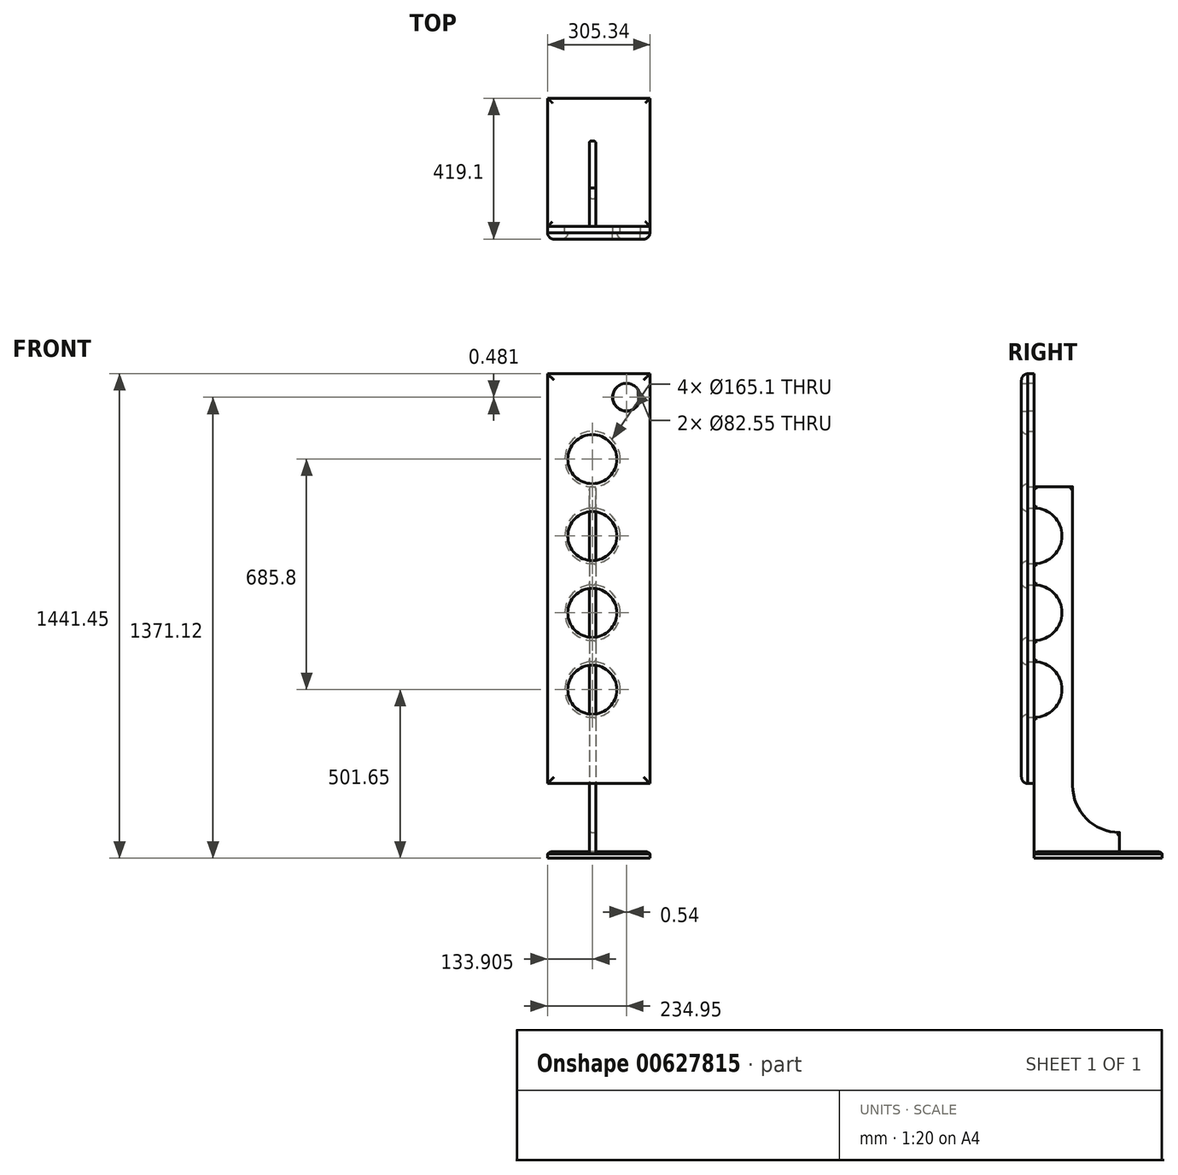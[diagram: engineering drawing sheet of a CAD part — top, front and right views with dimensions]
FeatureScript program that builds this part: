
annotation { "Feature Type Name" : "Feature", "Feature Type Description" : "" }
export const myFeature = defineFeature(function(context is Context, id is Id, definition is map)
    precondition{}
    {
        {
            var Q0;
            Q0=qCreatedBy(makeId("Front.planeOp"),FACE);
            var sketch = newSketch(context, id + "F0", { "sketchPlane" : qUnion([Q0])});
            skLineSegment(sketch, "E0.bottom", {"start": v(0, 0) * mm, "end": v(304.8, 0) * mm});
            skLineSegment(sketch, "E0.top", {"start": v(0, 1219.2) * mm, "end": v(304.8, 1219.2) * mm});
            skLineSegment(sketch, "E0.left", {"start": v(0, 0) * mm, "end": v(0, 1219.2) * mm});
            skLineSegment(sketch, "E0.right", {"start": v(304.8, 0) * mm, "end": v(304.8, 1219.2) * mm});
            skCircle(sketch, "E1", {"center": v(133.36, 965.2) * mm, "radius": 82.55 * mm});
            skCircle(sketch, "E2", {"center": v(133.36, 736.27) * mm, "radius": 82.55 * mm});
            skCircle(sketch, "E3", {"center": v(133.36, 508) * mm, "radius": 82.55 * mm});
            skCircle(sketch, "E4", {"center": v(133.36, 279.4) * mm, "radius": 82.55 * mm});
            skCircle(sketch, "E5", {"center": v(234.95, 1149.35) * mm, "radius": 41.28 * mm});
            skSolve(sketch);
        }
        {
            var Q0;
            Q0=makeQuery(id+"F0.imprint","IMPRINT",FACE,{"disambiguationData":[TD([[makeQuery(id+"F0.imprint","IMPRINT",EDGE,{"derivedFrom":sQuery(id+"F0.wireOp",EDGE,"E0.bottom")}),1.0]])]});
            extrude(context, id + "F1", {"entities" : qUnion([Q0]), "depth" : 19.05 * mm, "offsetDistance" : 25.4 * mm});
        }
        {
            var Q0;
            Q0=makeQuery(id+"F1.opExtrude","CAP_FACE",FACE,{"disambiguationData":[OSD([sQuery(id+"F0.wireOp",EDGE,"E0.bottom"),sQuery(id+"F0.wireOp",EDGE,"E0.top"),sQuery(id+"F0.wireOp",EDGE,"E0.left"),sQuery(id+"F0.wireOp",EDGE,"E0.right"),sQuery(id+"F0.wireOp",EDGE,"E1"),sQuery(id+"F0.wireOp",EDGE,"E2"),sQuery(id+"F0.wireOp",EDGE,"E3"),sQuery(id+"F0.wireOp",EDGE,"E4"),sQuery(id+"F0.wireOp",EDGE,"E5")])],"isStart":false});
            var sketch = newSketch(context, id + "F2", { "sketchPlane" : qUnion([Q0])});
            skLineSegment(sketch, "E6.bottom", {"start": v(-0.54, -0.48) * mm, "end": v(304.26, -0.48) * mm});
            skLineSegment(sketch, "E6.top", {"start": v(-0.54, 1218.72) * mm, "end": v(304.26, 1218.72) * mm});
            skLineSegment(sketch, "E6.left", {"start": v(-0.54, -0.48) * mm, "end": v(-0.54, 1218.72) * mm});
            skLineSegment(sketch, "E6.right", {"start": v(304.26, -0.48) * mm, "end": v(304.26, 1218.72) * mm});
            skCircle(sketch, "E7", {"center": v(132.82, 964.72) * mm, "radius": 73.03 * mm});
            skCircle(sketch, "E8", {"center": v(132.82, 735.79) * mm, "radius": 73.03 * mm});
            skCircle(sketch, "E9", {"center": v(132.82, 507.52) * mm, "radius": 73.03 * mm});
            skCircle(sketch, "E10", {"center": v(132.82, 278.92) * mm, "radius": 73.03 * mm});
            skCircle(sketch, "E11", {"center": v(234.4, 1148.87) * mm, "radius": 41.28 * mm});
            skSolve(sketch);
        }
        {
            var Q0;
            Q0 = qSketchRegion(id + "F2", true);
            extrude(context, id + "F3", {"entities" : qUnion([Q0]), "depth" : 19.05 * mm, "offsetDistance" : 25.4 * mm});
        }
        {
            var Q0;
            Q0=makeQuery(id+"F3.opExtrude","CAP_EDGE",EDGE,{"disambiguationData":[OSD([sQuery(id+"F2.wireOp",EDGE,"E7")])],"isStart":false});
            var Q1;
            Q1=makeQuery(id+"F3.opExtrude","CAP_EDGE",EDGE,{"disambiguationData":[OSD([sQuery(id+"F2.wireOp",EDGE,"E8")])],"isStart":false});
            var Q2;
            Q2=makeQuery(id+"F3.opExtrude","CAP_EDGE",EDGE,{"disambiguationData":[OSD([sQuery(id+"F2.wireOp",EDGE,"E9")])],"isStart":false});
            var Q3;
            Q3=makeQuery(id+"F3.opExtrude","CAP_EDGE",EDGE,{"disambiguationData":[OSD([sQuery(id+"F2.wireOp",EDGE,"E10")])],"isStart":false});
            fillet(context, id + "F4", {"entities" : qUnion([Q0, Q1, Q2, Q3]), "radius" : 19.05 * mm, "tangentPropagation" : true, "allowEdgeOverflow" : false});
        }
        {
            var Q0;
            Q0=makeQuery(id+"F3.opExtrude","CAP_EDGE",EDGE,{"disambiguationData":[OSD([sQuery(id+"F2.wireOp",EDGE,"E6.left")])],"isStart":false});
            var Q1;
            Q1=makeQuery(id+"F3.opExtrude","CAP_EDGE",EDGE,{"disambiguationData":[OSD([sQuery(id+"F2.wireOp",EDGE,"E6.top")])],"isStart":false});
            var Q2;
            Q2=makeQuery(id+"F3.opExtrude","CAP_EDGE",EDGE,{"disambiguationData":[OSD([sQuery(id+"F2.wireOp",EDGE,"E6.right")])],"isStart":false});
            var Q3;
            Q3=makeQuery(id+"F3.opExtrude","CAP_EDGE",EDGE,{"disambiguationData":[OSD([sQuery(id+"F2.wireOp",EDGE,"E6.bottom")])],"isStart":false});
            fillet(context, id + "F5", {"entities" : qUnion([Q0, Q1, Q2, Q3]), "radius" : 19.05 * mm, "tangentPropagation" : true, "allowEdgeOverflow" : false});
        }
        {
            var Q0;
            Q0=makeQuery(id+"F1.opExtrude","SWEPT_FACE",FACE,{"disambiguationData":[OSD([sQuery(id+"F0.wireOp",EDGE,"E0.left")])]});
            cPlane(context, id + "F6", {"entities" : qUnion([Q0]), "cplaneType" : CPlaneType.OFFSET, "offset" : 133.35 * mm, "oppositeDirection" : true, "width" : 152.4 * mm, "height" : 152.4 * mm});
        }
        {
            var Q0;
            Q0=qCreatedBy(id+"F6.planeOp",FACE);
            var sketch = newSketch(context, id + "F7", { "sketchPlane" : qUnion([Q0])});
            skArc(sketch, "E12", {"start": v(0, 819.15) * mm, "mid": v(-82.55, 736.6) * mm, "end": v(0, 654.05) * mm});
            skLineSegment(sketch, "E13", {"start": v(0, 819.15) * mm, "end": v(0, 882.65) * mm});
            skLineSegment(sketch, "E14", {"start": v(0, 882.65) * mm, "end": v(-114.3, 882.65) * mm});
            skLineSegment(sketch, "E15", {"start": v(0, 654.05) * mm, "end": v(0, 590.55) * mm});
            skArc(sketch, "E16", {"start": v(0, 590.55) * mm, "mid": v(-82.55, 508) * mm, "end": v(0, 425.45) * mm});
            skLineSegment(sketch, "E17", {"start": v(0, 425.45) * mm, "end": v(0, 361.95) * mm});
            skArc(sketch, "E18", {"start": v(0, 361.95) * mm, "mid": v(-82.55, 279.4) * mm, "end": v(0, 196.85) * mm});
            skLineSegment(sketch, "E19", {"start": v(0, 196.85) * mm, "end": v(0, -209.55) * mm});
            skLineSegment(sketch, "E20", {"start": v(0, -209.55) * mm, "end": v(-254, -209.55) * mm});
            skLineSegment(sketch, "E21", {"start": v(-114.3, 882.65) * mm, "end": v(-114.3, -6.35) * mm});
            skLineSegment(sketch, "E22", {"start": v(-254, -209.55) * mm, "end": v(-254, -146.05) * mm});
            skArc(sketch, "E23", {"start": v(-254, -146.05) * mm, "mid": v(-155.22, -105.13) * mm, "end": v(-114.3, -6.35) * mm});
            skSolve(sketch);
        }
        {
            var Q0;
            Q0 = qSketchRegion(id + "F7", true);
            extrude(context, id + "F8", {"entities" : qUnion([Q0]), "depth" : 19.05 * mm, "offsetDistance" : 25.4 * mm, "symmetric" : true});
        }
        {
            var Q0;
            Q0=makeQuery(id+"F8.opExtrude","CAP_FACE",FACE,{"disambiguationData":[OSD([sQuery(id+"F7.wireOp",EDGE,"E12"),sQuery(id+"F7.wireOp",EDGE,"E13"),sQuery(id+"F7.wireOp",EDGE,"E14"),sQuery(id+"F7.wireOp",EDGE,"E15"),sQuery(id+"F7.wireOp",EDGE,"E16"),sQuery(id+"F7.wireOp",EDGE,"E17"),sQuery(id+"F7.wireOp",EDGE,"E18"),sQuery(id+"F7.wireOp",EDGE,"E19"),sQuery(id+"F7.wireOp",EDGE,"E20"),sQuery(id+"F7.wireOp",EDGE,"E21"),sQuery(id+"F7.wireOp",EDGE,"E22"),sQuery(id+"F7.wireOp",EDGE,"E23")])],"isStart":true});
            var Q1;
            Q1=makeQuery(id+"F8.opExtrude","CAP_FACE",FACE,{"disambiguationData":[OSD([sQuery(id+"F7.wireOp",EDGE,"E12"),sQuery(id+"F7.wireOp",EDGE,"E13"),sQuery(id+"F7.wireOp",EDGE,"E14"),sQuery(id+"F7.wireOp",EDGE,"E15"),sQuery(id+"F7.wireOp",EDGE,"E16"),sQuery(id+"F7.wireOp",EDGE,"E17"),sQuery(id+"F7.wireOp",EDGE,"E18"),sQuery(id+"F7.wireOp",EDGE,"E19"),sQuery(id+"F7.wireOp",EDGE,"E20"),sQuery(id+"F7.wireOp",EDGE,"E21"),sQuery(id+"F7.wireOp",EDGE,"E22"),sQuery(id+"F7.wireOp",EDGE,"E23")])],"isStart":false});
            fillet(context, id + "F9", {"entities" : qUnion([Q0, Q1]), "radius" : 6.35 * mm, "tangentPropagation" : true, "allowEdgeOverflow" : false});
        }
        {
            var Q0;
            Q0=makeQuery(id+"F8.opExtrude","SWEPT_FACE",FACE,{"disambiguationData":[OSD([sQuery(id+"F7.wireOp",EDGE,"E20")])]});
            var sketch = newSketch(context, id + "F10", { "sketchPlane" : qUnion([Q0])});
            skLineSegment(sketch, "E24.bottom", {"start": v(0, 0) * mm, "end": v(304.8, 0) * mm});
            skLineSegment(sketch, "E24.top", {"start": v(0, -381) * mm, "end": v(304.8, -381) * mm});
            skLineSegment(sketch, "E24.left", {"start": v(0, 0) * mm, "end": v(0, -381) * mm});
            skLineSegment(sketch, "E24.right", {"start": v(304.8, 0) * mm, "end": v(304.8, -381) * mm});
            skSolve(sketch);
        }
        {
            var Q0;
            Q0 = qSketchRegion(id + "F10", true);
            extrude(context, id + "F11", {"entities" : qUnion([Q0]), "depth" : 12.7 * mm, "offsetDistance" : 25.4 * mm});
        }
        {
            var Q0;
            Q0 = qSketchRegion(id + "F10", true);
            extrude(context, id + "F12", {"entities" : qUnion([Q0]), "oppositeDirection" : true, "depth" : 6.35 * mm, "offsetDistance" : 25.4 * mm});
        }
        {
            var Q0;
            Q0=makeQuery(id+"F12.opExtrude","CAP_FACE",FACE,{"disambiguationData":[OSD([sQuery(id+"F10.wireOp",EDGE,"E24.bottom"),sQuery(id+"F10.wireOp",EDGE,"E24.top"),sQuery(id+"F10.wireOp",EDGE,"E24.left"),sQuery(id+"F10.wireOp",EDGE,"E24.right")])],"isStart":false});
            fillet(context, id + "F13", {"entities" : qUnion([Q0]), "radius" : 19.05 * mm, "tangentPropagation" : true, "allowEdgeOverflow" : false});
        }
        {
            var Q0;
            Q0=makeQuery(id+"F8.opExtrude","SWEPT_BODY",BODY,{"disambiguationData":[OSD([sQuery(id+"F7.wireOp",EDGE,"E12"),sQuery(id+"F7.wireOp",EDGE,"E13"),sQuery(id+"F7.wireOp",EDGE,"E14"),sQuery(id+"F7.wireOp",EDGE,"E15"),sQuery(id+"F7.wireOp",EDGE,"E16"),sQuery(id+"F7.wireOp",EDGE,"E17"),sQuery(id+"F7.wireOp",EDGE,"E18"),sQuery(id+"F7.wireOp",EDGE,"E19"),sQuery(id+"F7.wireOp",EDGE,"E20"),sQuery(id+"F7.wireOp",EDGE,"E21"),sQuery(id+"F7.wireOp",EDGE,"E22"),sQuery(id+"F7.wireOp",EDGE,"E23")])]});
            var Q1;
            Q1=makeQuery(id+"F11.opExtrude","SWEPT_BODY",BODY,{"disambiguationData":[OSD([sQuery(id+"F10.wireOp",EDGE,"E24.bottom"),sQuery(id+"F10.wireOp",EDGE,"E24.top"),sQuery(id+"F10.wireOp",EDGE,"E24.left"),sQuery(id+"F10.wireOp",EDGE,"E24.right")])]});
            booleanBodies(context, id + "F14", {"operationType" : BooleanOperationType.SUBTRACTION, "tools" : qUnion([Q0]), "targets" : qUnion([Q1]), "keepTools" : true});
        }
    });
